# Revit family: 265-91-001 DN1200
name_source: partatom
category: Pipe Accessories
units: mm (PartAtom-declared; Revit-internal decimal feet)

## family parameters
Always vertical = Yes
Cut with Voids When Loaded = No
Part Type = Valve - Breaks Into
Round Connector Dimension = Use Diameter
Shared = No
Work Plane-Based = No

## types (2) — shared parameters
25 = 25 mm  [stored 0.082021 ft]
Bolt.no = 32 mm  [stored 0.104987 ft]
Bore = 600 mm  [stored 1.9685 ft]
DN = 1200 mm  [stored 3.93701 ft]
Description_ = AVK DISMANTLING JOINT WITH CENTRE FLANGE, PN10/16
Raised_dis = 5 mm  [stored 0.0164042 ft]
Search_table = 265-91-001 DN1200
URL_product_pages = https://www.avkvalves.com
zero-valued in all types: Default Elevation

## per-type parameters (varying)
| type | B1 | D | DN1200_PN10 | DN1200_PN16 | FL_T | FL_T/2 | L | L1 | L11 | L2 | L3 | Nut_T | PCD | PN | S | S11 | T | T1 | offset | raised_R |
| DN1200_PN16 | 51 mm | 745 mm  [stored 2.44423 ft] | 265-9-0350-11-04036401 | 265-9-0350-10-14036400 | 57 mm  [stored 0.187008 ft] | 29 mm | 640 mm  [stored 2.09974 ft] | 245 mm | 360 mm  [stored 1.1811 ft] | 42 mm | 29 mm | 17 mm | 671 mm | 16 mm  [stored 0.0524934 ft] | 45 mm  [stored 0.147638 ft] | 61 mm | 17 mm | 43 mm  [stored 0.141076 ft] | 16 mm  [stored 0.0524934 ft] | 648 mm |
| DN1200_PN10 | 44 mm | 728 mm | 265-9-1200-11-04036401 | 265-9-1200-10-14036400 | 45 mm  [stored 0.147638 ft] | 23 mm | 545 mm  [stored 1.78806 ft] | 218 mm | 320 mm  [stored 1.04987 ft] | 35 mm  [stored 0.114829 ft] | 23 mm | 14 mm  [stored 0.0459318 ft] | 655 mm | 10 mm  [stored 0.0328084 ft] | 36 mm  [stored 0.11811 ft] | 49 mm | 14 mm  [stored 0.0459318 ft] | 34 mm | 13 mm  [stored 0.0426509 ft] | 633 mm |

note: [stored X ft] marks values corroborated as IEEE doubles in the binary element streams (Revit-internal decimal feet)

## geometry (parser evidence)
native form markers: Sweep x9
no freeform markers — native parametric forms only
